# Revit family: IS_iLifeA_T4521_BIM_NL
name_source: partatom
category: Plumbing Fixtures
units: mm (PartAtom-declared; Revit-internal decimal feet)

## family parameters
Always vertical = No
Cut with Voids When Loaded = No
OmniClass Number = 23.45.05.14.14
OmniClass Title = Sinks/Lavatories
Part Type = Normal
Room Calculation Point = No
Round Connector Dimension = Use Diameter
Shared = No
Work Plane-Based = No

## types (2) — shared parameters
Accessories = https://www.idealstandard.nl
Afmetingen = 260 x 340 x 173mm
AfstandsEenheid = Millimeter
AreaMeasurement = internal
AreaUnits = Millimeter
Auteur = Ideal Standard
BIMObjectName = IS_IdealStandard_Pedestalwashbasins_I.life_T4521
Beschrijvinggarantie = Herstellergarantie
BimObjectNaam = IS_IdealStandard_Pedestalwashbasins_I.life_T4521
Brand url = https://www.idealstandard.nl
ConnectionType = Plumbing
CurrencyUnit = €
CurrentRevision = 1
Date of publishing = 28/06/2021
DurationUnit = Years
DuurEenheid = Jaar
Edition number = 1
Garantieonderdelen = 5
Garantieunits = Jaar
Help = https://www.idealstandard.nl
Hoogte = 340.00003
Hulp = https://www.idealstandard.nl
IFC Classification = Sanitary Terminal
IfcExportAs = IfcSanitaryTerminalType
IfcExportType = PEDESTAL
Installatieinstructies = https://www.idealstandard.nl
Installation instructions = https://www.idealstandard.nl
InstallationInstructions = https://www.idealstandard.nl
Lengte = 260 mm
LinearUnits = millimeter
MaintenanceInformation = https://www.idealstandard.nl
Manufacturer = Ideal Standard
Manufacturer name = Ideal Standard
ManufacturerURL = https://www.idealstandard.nl
Material = Vitrous China
Material main = Vitrous China
Merk = Ideal Standard
Montageinstuctie = Wandhangende wastafels
Name = Pedestalwashbasins_I.life_T4521_IdealStandard
NettWeight = 6
NominalDepth = 260 mm
NominalHeight = 340 mm
NominalWidth = 173 mm
Normen = Pedestalwashbasins_I.life_T4521_IdealStandard
Ophangingwastafel = Wandhangende wastafels
OppervlakteEenheid = millimeter
Product Guid = 752ffc23-e4db-45b9-9682-5b9cdcf157b7
Product SKU = T4521
Product certification = https://www.idealstandard.nl
Product data url = https://bimobject.com
Product family = I.life
Product group = Semi Pedestal
Product name = I.life A semipedestal for handrinse white
Product url = https://www.idealstandard.nl
ProductInformation = https://www.idealstandard.nl
ProductSoort = Wastafel
Productinformatie = https://www.idealstandard.nl
QR code = http://bimobject.com
Referentie = I.life A semipedestal for handrinse white
Revisie = 1
Shape = sculpture
Size = 260 x 340 x 173mm
Space = Internal
SpareParts = https://www.idealstandard.nl
Technical description = https://www.idealstandard.nl
Telefoonnummer = 077 355 08 08
Typeconnectie = loodgieter
Typewastafel = wandhangende wastafel
URL = https://https:
Uniclass2015Beschrijving = Pedestal washbasins
Uniclass2015Code = Pr_40_20_96_63
Uniclass2015Referentie = Pr_40_20_96_63
Uniclass2015Title = Pedestal washbasins
Uniclass2015Version = v1.20
Urlproducent = https://https:
ValutaEenheid = €
Versie = 1
Version = 1
VolumeUnits = liters
Volumeunits = liters
Vorm = beeldhouwwerk
WRASURL = https://www.wrasapprovals.co.uk
WaarborgGarantieInstallatie = https://www.idealstandard.nl
WarrantyDescription = manufacturer warranty
WarrantyDurationParts = 99
WarrantyDurationUnit = years
Wisselstukken = https://www.idealstandard.nl
Youtube clip = https://www.youtube.com
zero-valued in all types: Breedte, BrutoGewicht, Cost, Diepte, DrainSize, GrootteAfvoergat, Nettogewicht, Overloop, Vervangingskosten

## per-type parameters (varying)
| type | Afwerking | Artikelnummer | Artikelomschrijving | Artikelreferentie | BarCode | Bestanddelen | Color | Description | Eigenschappen | Features | Finish | GTIN code | Kleur | MainColor | Model | ModelNumber | ModelReference |
| T4521MA - I.life A semipedestal white IP - Ideal Plus White | IdealPlusWeiß | T4521MA | I.life A semi-voetstuk wit IP - Ideal Plus White | I.life A semipedestal white IP | 8014140486732 | Halbpodest weiß IP | IdealPlusWeiß | I.life A semi-voetstuk wit IP - Ideal Plus White | Halbpodest weiß IP | Halbpodest weiß IP | IdealPlusWeiß | https://8014140486732 | IdealPlusWeiß | IdealPlusWeiß | T4521MA | T4521MA | I.life A semipedestal white IP |
| T452101 - I.life A semipedestal for handrinse white - White | Weiß | T452101 | I.life Een semi-sokkel voor handspoeling wit - Wit | I.life A semipedestal for handrinse white | 8014140485896 | Halbpodest für Handspüler weiß | Weiß | I.life Een semi-sokkel voor handspoeling wit - Wit | Halbpodest für Handspüler weiß | Halbpodest für Handspüler weiß | Weiß | https://8014140485896 | Weiß | Weiß | T452101 | T452101 | I.life A semipedestal for handrinse white |

## geometry (parser evidence)
native form markers: Sweep x3
no freeform markers — native parametric forms only
